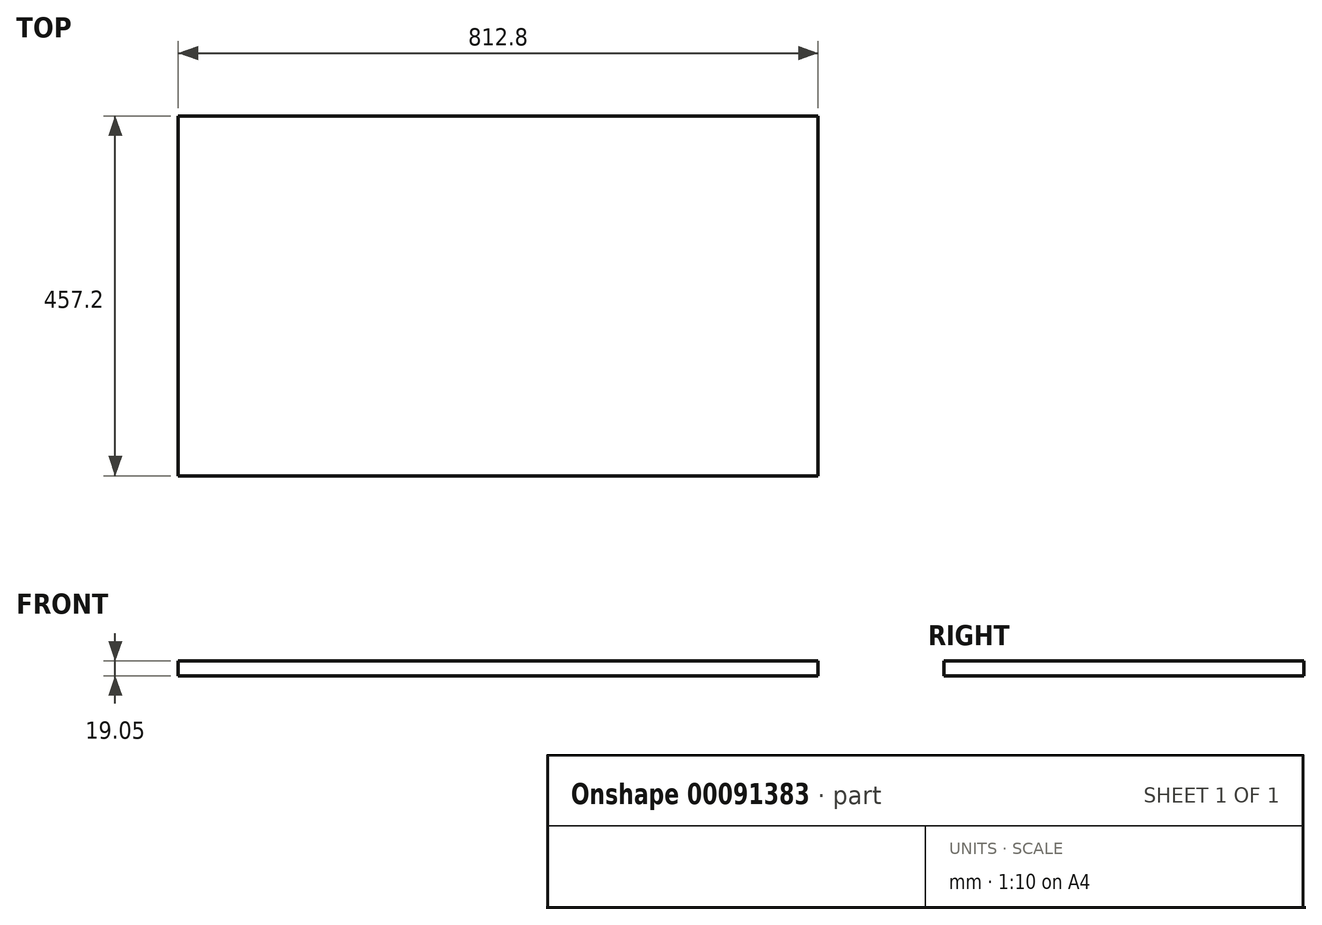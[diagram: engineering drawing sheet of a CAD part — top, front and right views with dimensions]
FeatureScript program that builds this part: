
annotation { "Feature Type Name" : "Feature", "Feature Type Description" : "" }
export const myFeature = defineFeature(function(context is Context, id is Id, definition is map)
    precondition{}
    {
        {
            var Q0;
            Q0=qCreatedBy(makeId("Top.planeOp"),FACE);
            var sketch = newSketch(context, id + "F0", { "sketchPlane" : qUnion([Q0])});
            skLineSegment(sketch, "E0.bottom", {"start": v(-406.4, 228.6) * mm, "end": v(406.4, 228.6) * mm});
            skLineSegment(sketch, "E0.top", {"start": v(-406.4, -228.6) * mm, "end": v(406.4, -228.6) * mm});
            skLineSegment(sketch, "E0.left", {"start": v(-406.4, 228.6) * mm, "end": v(-406.4, -228.6) * mm});
            skLineSegment(sketch, "E0.right", {"start": v(406.4, 228.6) * mm, "end": v(406.4, -228.6) * mm});
            skPoint(sketch, "E0.middle", {"position": v(0, 0) * mm});
            skSolve(sketch);
        }
        {
            var Q0;
            Q0=makeQuery(id+"F0.imprint","IMPRINT",FACE,{"disambiguationData":[TD([[makeQuery(id+"F0.imprint","IMPRINT",EDGE,{"derivedFrom":sQuery(id+"F0.wireOp",EDGE,"E0.bottom")}),-1.0]])]});
            extrude(context, id + "F1", {"entities" : qUnion([Q0]), "depth" : 19.05 * mm});
        }
    });
